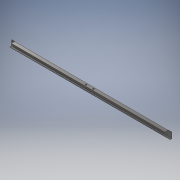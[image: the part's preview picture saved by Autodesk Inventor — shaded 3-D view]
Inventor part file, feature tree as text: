
AUTODESK INVENTOR PART (.ipt)
format: ipt  version: 2017 (Build 210142000, 142)  size: 185,856 bytes
history: native  units: mm
features: sheet_metal_op x7, other x6, sketch x4, reference x2, extrude x1, chamfer x1
ambient origin geometry x8: Origin, YZ Plane, XZ Plane, XY Plane, X Axis, Y Axis, Z Axis, Center Point
bodies: Body1 (feature_tree)
feature tree (21):
  sheet_metal_op  "Face1"
  sheet_metal_op  "Flange1"
  sheet_metal_op  "Flange2"
  extrude  "Extrusion1"  Depth=30.0mm
  chamfer  "Chamfer1"  Distance=3.0mm
  sketch  "Sketch2"  dims[d12=860.598mm d13=30.0mm]
  other  "Plate2"
  sketch  "Sketch3"  dims[d14=1.5mm]
  other  "Plate3"
  sheet_metal_op  "Bend2"
  sheet_metal_op  "Corner2"
  sketch  "Sketch4"  dims[d15=1.5mm]
  other  "Plate4"
  sheet_metal_op  "Bend3"
  sheet_metal_op  "Corner3"
  sketch  "Sketch5"  dims[d16=0.75mm d17=3.0mm d18=1.5mm d19=823.598mm d20=20.0mm d21=90.0deg d22=1.5mm d23=6.0mm d24=1.5mm d25=1.5mm d26=1.5mm d27=0.75mm d28=3.0mm d29=1.5mm d30=10.0mm d31=90.0deg d32=1.5mm d33=6.0mm d34=1.5mm d35=1.5mm d36=5.5mm d37=5.5mm d38=1.5mm d39=0.0mm d40=1.5mm d41=2.0mm d42=45.0deg]
  reference  "Reference1"
  reference  "Reference2"
  other  "Definition1"
  other  "Bancada de Lavagem Mãos - 1150 x 370 x 900h.iam"
  other  "Atrack 60 x 20 x 10:1"
